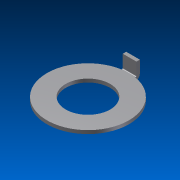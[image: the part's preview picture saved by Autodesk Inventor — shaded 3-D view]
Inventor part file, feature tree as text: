
AUTODESK INVENTOR PART (.ipt)
format: ipt  version: 2011 SP1 (Build 150282100, 282)  size: 105,984 bytes
history: native  units: mm
features: extrude x3, sketch x3, projected_geometry x1
ambient origin geometry x8: Origin, YZ Plane, XZ Plane, XY Plane, X Axis, Y Axis, Z Axis, Center Point
bodies: Solid1 (feature_tree)
feature tree (7):
  extrude  "Extrusion1"  Depth=6.5mm
  extrude  "Extrusion2"  Depth=0.2mm
  extrude  "Extrusion3"  Depth=2.4mm
  sketch  "Sketch1"  dims[d0=12.0mm d1=6.5mm]
  sketch  "Sketch2"  dims[d2=0.5mm d3=0.0mm d6=0.2mm]
  sketch  "Sketch3"  dims[d7=0.5mm d8=2.4mm d9=2.0mm d10=0.0mm d11=0.5mm d12=0.0mm]
  projected_geometry  "Projected Loop1"
